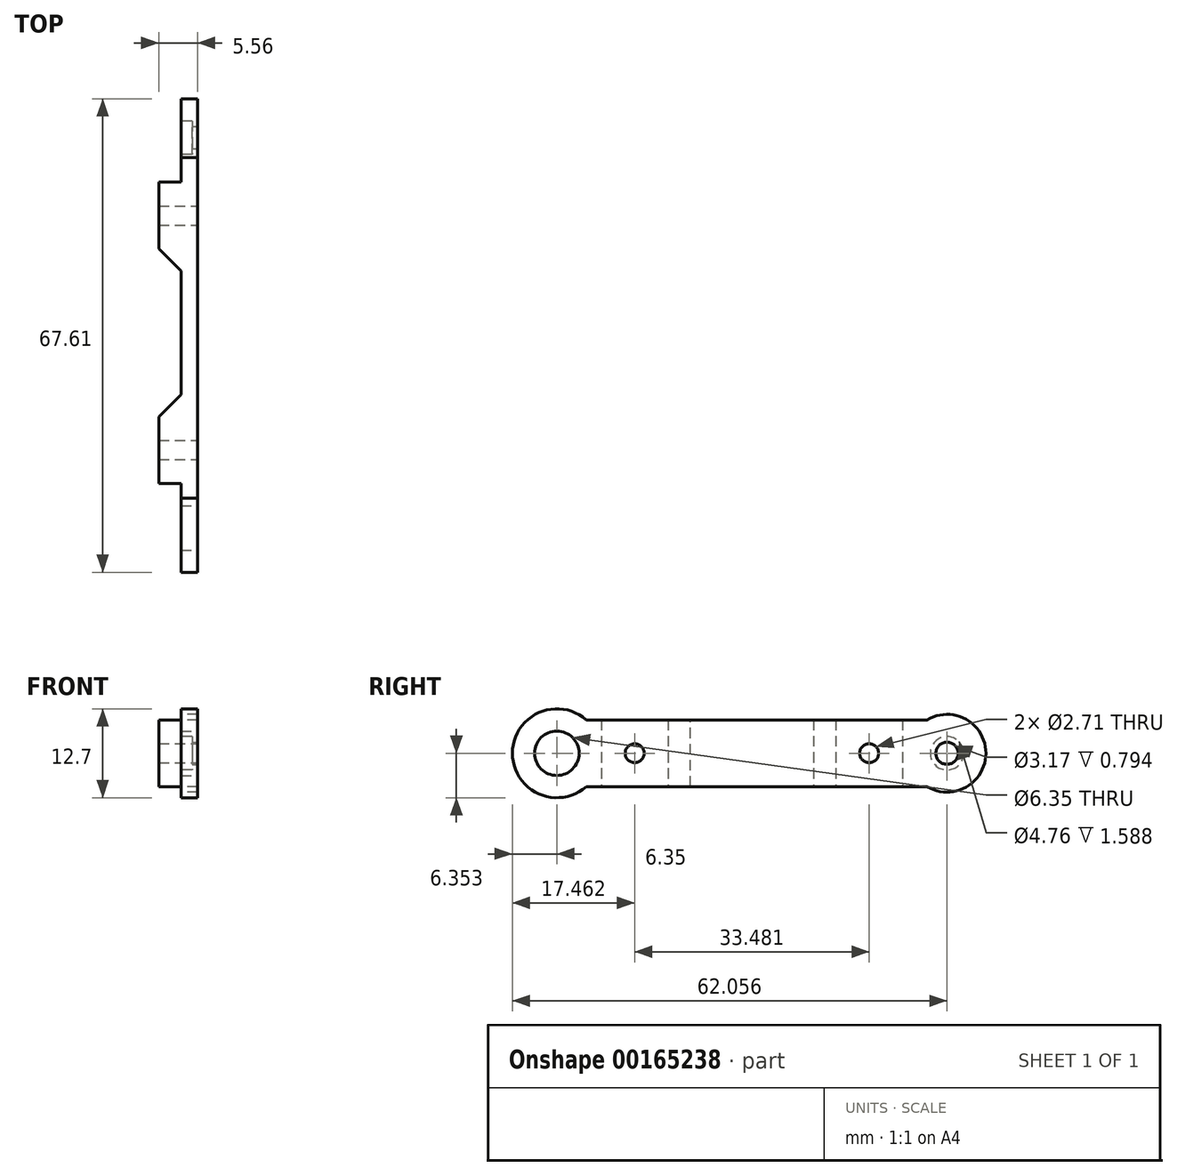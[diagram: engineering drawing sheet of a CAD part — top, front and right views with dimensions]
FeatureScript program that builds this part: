
annotation { "Feature Type Name" : "Feature", "Feature Type Description" : "" }
export const myFeature = defineFeature(function(context is Context, id is Id, definition is map)
    precondition{}
    {
        {
            var Q0;
            Q0=qCreatedBy(makeId("Top.planeOp"),FACE);
            var sketch = newSketch(context, id + "F0", { "sketchPlane" : qUnion([Q0])});
            skLineSegment(sketch, "E0.top", {"start": v(0, 55.7) * mm, "end": v(-2.38, 55.7) * mm});
            skLineSegment(sketch, "E0.left", {"start": v(0, 0) * mm, "end": v(0, 55.7) * mm});
            skLineSegment(sketch, "E0.right", {"start": v(-2.38, 49.36) * mm, "end": v(-2.38, 55.7) * mm});
            skLineSegment(sketch, "E1", {"start": v(0, 0) * mm, "end": v(-2.38, 0) * mm});
            skLineSegment(sketch, "E2", {"start": v(-2.38, 0) * mm, "end": v(-2.38, 6.35) * mm});
            skLineSegment(sketch, "E3", {"start": v(-2.38, 6.35) * mm, "end": v(-5.56, 6.35) * mm});
            skLineSegment(sketch, "E4", {"start": v(-5.56, 6.35) * mm, "end": v(-5.56, 15.87) * mm});
            skLineSegment(sketch, "E5", {"start": v(-5.56, 15.87) * mm, "end": v(-2.38, 15.87) * mm});
            skLineSegment(sketch, "E6", {"start": v(-2.38, 15.87) * mm, "end": v(-2.38, 39.83) * mm});
            skLineSegment(sketch, "E7", {"start": v(-2.38, 39.83) * mm, "end": v(-5.56, 39.83) * mm});
            skLineSegment(sketch, "E8", {"start": v(-5.56, 39.83) * mm, "end": v(-5.56, 49.36) * mm});
            skLineSegment(sketch, "E9", {"start": v(-5.56, 49.36) * mm, "end": v(-2.38, 49.36) * mm});
            skLineSegment(sketch, "E10", {"start": v(-2.38, 27.85) * mm, "end": v(0, 27.85) * mm, "construction": true});
            skSolve(sketch);
        }
        {
            var Q0;
            Q0=qSketchRegion(id+"F0",true);
            extrude(context, id + "F1", {"entities" : qUnion([Q0]), "depth" : 9.52 * mm});
        }
        {
            var Q0;
            Q0=makeQuery(id+"F1.opExtrude","SWEPT_FACE",FACE,{"disambiguationData":[OSD([sQuery(id+"F0.wireOp",EDGE,"E0.right")])]});
            var sketch = newSketch(context, id + "F2", { "sketchPlane" : qUnion([Q0])});
            skCircle(sketch, "E11", {"center": v(-55.7, 4.76) * mm, "radius": 5.56 * mm});
            skCircle(sketch, "E12", {"center": v(0, 4.76) * mm, "radius": 6.35 * mm});
            skSolve(sketch);
        }
        {
            var Q0;
            Q0=qSketchRegion(id+"F2",true);
            var Q1;
            Q1=makeQuery(id+"F1.opExtrude","SWEPT_FACE",FACE,{"disambiguationData":[OSD([sQuery(id+"F0.wireOp",EDGE,"E0.left")])]});
            extrude(context, id + "F3", {"entities" : qUnion([Q0]), "operationType" : NewBodyOperationType.ADD, "endBound" : BoundingType.UP_TO_SURFACE, "oppositeDirection" : true, "endBoundEntityFace" : qUnion([Q1]), "depth" : 25.4 * mm});
        }
        {
            var Q0;
            Q0=makeQuery(id+"F3.boolean.opBoolean","MERGE",FACE,{"derivedFrom":[makeQuery(id+"F1.opExtrude","SWEPT_FACE",FACE,{"disambiguationData":[OSD([sQuery(id+"F0.wireOp",EDGE,"E0.left")])]}),makeQuery(id+"F3.opExtrude","CAP_FACE",FACE,{"disambiguationData":[OSD([sQuery(id+"F2.wireOp",EDGE,"E11")])],"isStart":false}),makeQuery(id+"F3.opExtrude","CAP_FACE",FACE,{"disambiguationData":[OSD([sQuery(id+"F2.wireOp",EDGE,"E12")])],"isStart":false})]});
            var sketch = newSketch(context, id + "F4", { "sketchPlane" : qUnion([Q0])});
            skCircle(sketch, "E13", {"center": v(0, 4.76) * mm, "radius": 3.18 * mm});
            skLineSegment(sketch, "E14", {"start": v(11.11, 9.52) * mm, "end": v(11.11, 0) * mm, "construction": true});
            skLineSegment(sketch, "E15", {"start": v(44.6, 9.53) * mm, "end": v(44.6, 0) * mm, "construction": true});
            skCircle(sketch, "E16", {"center": v(11.11, 4.76) * mm, "radius": 1.35 * mm});
            skCircle(sketch, "E17", {"center": v(44.6, 4.76) * mm, "radius": 1.35 * mm});
            skCircle(sketch, "E18", {"center": v(55.7, 4.76) * mm, "radius": 1.59 * mm});
            skSolve(sketch);
        }
        {
            var Q0;
            Q0=qSketchRegion(id+"F4",true);
            var Q1;
            Q1=makeQuery(id+"F1.opExtrude","SWEPT_FACE",FACE,{"disambiguationData":[OSD([sQuery(id+"F0.wireOp",EDGE,"E4")])]});
            extrude(context, id + "F5", {"entities" : qUnion([Q0]), "operationType" : NewBodyOperationType.REMOVE, "endBound" : BoundingType.UP_TO_SURFACE, "oppositeDirection" : true, "endBoundEntityFace" : qUnion([Q1]), "depth" : 25.4 * mm});
        }
        {
            var Q0;
            Q0=makeQuery(id+"F3.boolean.opBoolean","MERGE",FACE,{"derivedFrom":[makeQuery(id+"F1.opExtrude","SWEPT_FACE",FACE,{"disambiguationData":[OSD([sQuery(id+"F0.wireOp",EDGE,"E0.right")])]}),makeQuery(id+"F3.opExtrude","CAP_FACE",FACE,{"disambiguationData":[OSD([sQuery(id+"F2.wireOp",EDGE,"E11")])],"isStart":true})]});
            var sketch = newSketch(context, id + "F6", { "sketchPlane" : qUnion([Q0])});
            skCircle(sketch, "E19", {"center": v(-55.7, 4.76) * mm, "radius": 2.38 * mm});
            skSolve(sketch);
        }
        {
            var Q0;
            Q0=qSketchRegion(id+"F6",true);
            extrude(context, id + "F7", {"entities" : qUnion([Q0]), "operationType" : NewBodyOperationType.REMOVE, "oppositeDirection" : true, "depth" : 1.59 * mm});
        }
        {
            var Q0;
            Q0=makeQuery(id+"F1.opExtrude","SWEPT_EDGE",EDGE,{"disambiguationData":[OSD([sQuery(id+"F0.wireOp",EDGE,"E6"),sQuery(id+"F0.wireOp",EDGE,"E7")])]});
            var Q1;
            Q1=makeQuery(id+"F1.opExtrude","SWEPT_EDGE",EDGE,{"disambiguationData":[OSD([sQuery(id+"F0.wireOp",EDGE,"E5"),sQuery(id+"F0.wireOp",EDGE,"E6")])]});
            chamfer(context, id + "F8", {"entities" : qUnion([Q0, Q1]), "width" : 3.17 * mm, "tangentPropagation" : true});
        }
    });
